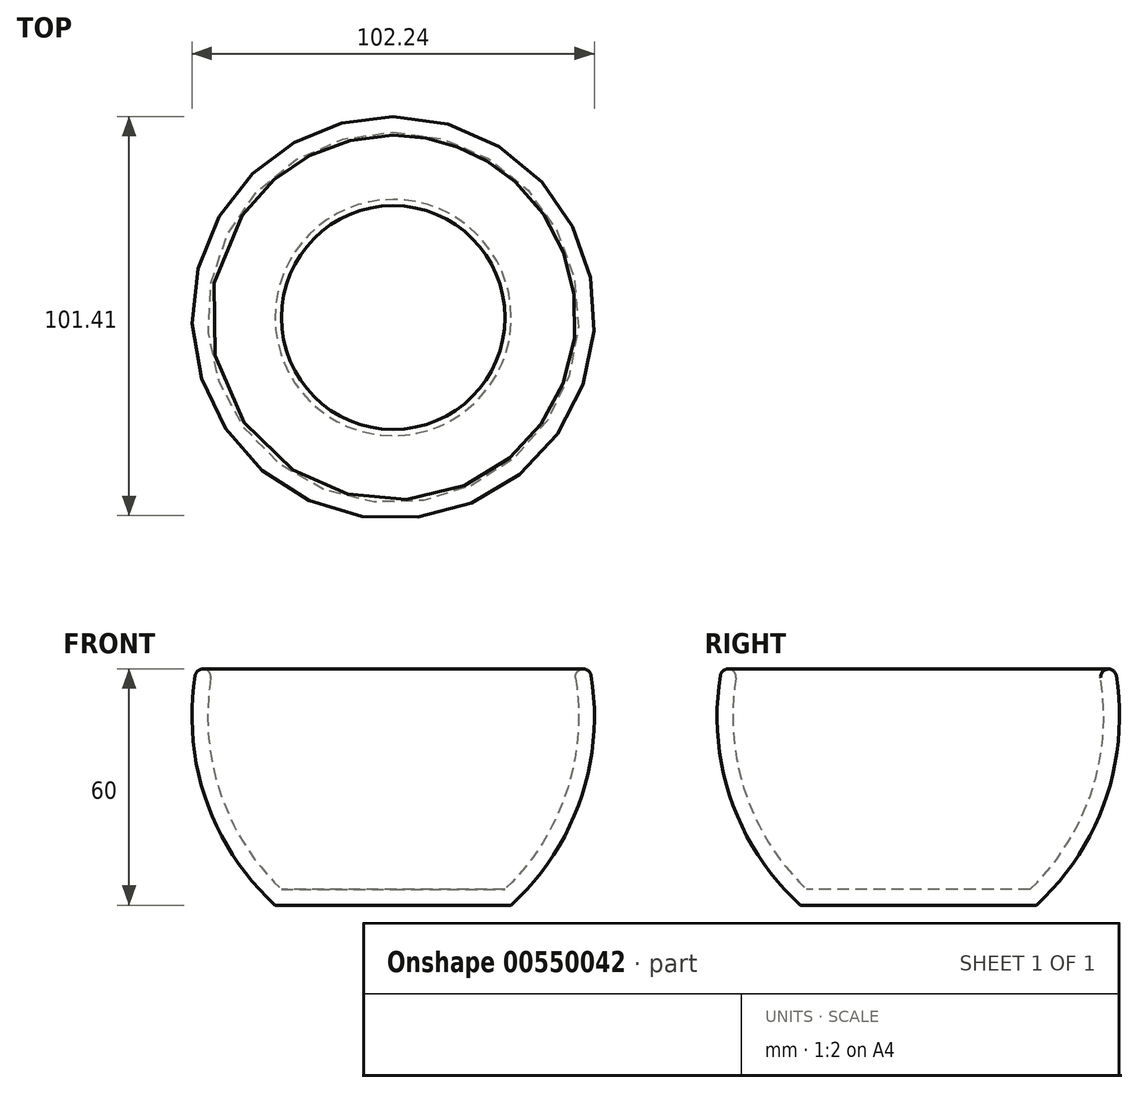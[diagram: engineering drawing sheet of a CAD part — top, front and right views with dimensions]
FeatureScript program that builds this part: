
annotation { "Feature Type Name" : "Feature", "Feature Type Description" : "" }
export const myFeature = defineFeature(function(context is Context, id is Id, definition is map)
    precondition{}
    {
        {
            var Q0;
            Q0=qCreatedBy(makeId("Top.planeOp"),FACE);
            var sketch = newSketch(context, id + "F0", { "sketchPlane" : qUnion([Q0])});
            skLineSegment(sketch, "E0", {"start": v(0, 0) * mm, "end": v(30, 0) * mm});
            skLineSegment(sketch, "E1", {"start": v(0, 60) * mm, "end": v(50, 60) * mm});
            skArc(sketch, "E2", {"start": v(30, 0) * mm, "mid": v(47.78, 27.4) * mm, "end": v(50, 60) * mm});
            skLineSegment(sketch, "E3", {"start": v(0, 0) * mm, "end": v(0, 60) * mm});
            skSolve(sketch);
        }
        {
            var Q0;
            Q0=makeQuery(id+"F0.imprint","IMPRINT",FACE,{"disambiguationData":[TD([[makeQuery(id+"F0.imprint","IMPRINT",EDGE,{"derivedFrom":sQuery(id+"F0.wireOp",EDGE,"E0")}),1.0]])]});
            var Q1;
            Q1=sQuery(id+"F0.wireOp",EDGE,"E3");
            revolve(context, id + "F1", {"entities" : qUnion([Q0]), "axis" : qUnion([Q1]), "revolveType" : RevolveType.FULL});
        }
        {
            var Q0;
            Q0=makeQuery(id+"F1.opRevolve","SWEPT_FACE",FACE,{"disambiguationData":[OSD([sQuery(id+"F0.wireOp",EDGE,"E1")])]});
            shell(context, id + "F2", {"entities" : qUnion([Q0]), "thickness" : 4 * mm});
        }
        {
            var Q0;
            Q0=qCreatedBy(makeId("Front.planeOp"),FACE);
            var sketch = newSketch(context, id + "F3", { "sketchPlane" : qUnion([Q0])});
            skLineSegment(sketch, "E4", {"start": v(-75.17, 0) * mm, "end": v(74.74, 0) * mm, "construction": true});
            skSolve(sketch);
        }
        {
            var Q0;
            Q0=makeQuery(id+"F1.opRevolve","SWEPT_BODY",BODY,{"disambiguationData":[OSD([sQuery(id+"F0.wireOp",EDGE,"E0"),sQuery(id+"F0.wireOp",EDGE,"E1"),sQuery(id+"F0.wireOp",EDGE,"E2"),sQuery(id+"F0.wireOp",EDGE,"E3")])]});
            var Q1;
            Q1=sQuery(id+"F3.wireOp",EDGE,"E4");
            transform(context, id + "F4", {"entities" : qUnion([Q0]), "transformType" : TransformType.ROTATION, "transformAxis" : qUnion([Q1]), "angle" : 90 * degree, "makeCopy" : false});
        }
        {
            var Q0;
            Q0=makeQuery(id+"F2.opShell","OFFSET_EDGE",EDGE,{"disambiguationData":[OSD([sQuery(id+"F0.wireOp",EDGE,"E1"),sQuery(id+"F0.wireOp",EDGE,"E2")])]});
            fillet(context, id + "F5", {"entities" : qUnion([Q0]), "radius" : 2 * mm, "tangentPropagation" : true, "allowEdgeOverflow" : false});
        }
        {
            var Q0;
            Q0=makeQuery(id+"F1.opRevolve","SWEPT_EDGE",EDGE,{"disambiguationData":[OSD([sQuery(id+"F0.wireOp",EDGE,"E1"),sQuery(id+"F0.wireOp",EDGE,"E2")])]});
            fillet(context, id + "F6", {"entities" : qUnion([Q0]), "radius" : 2 * mm, "tangentPropagation" : true, "allowEdgeOverflow" : false});
        }
    });
